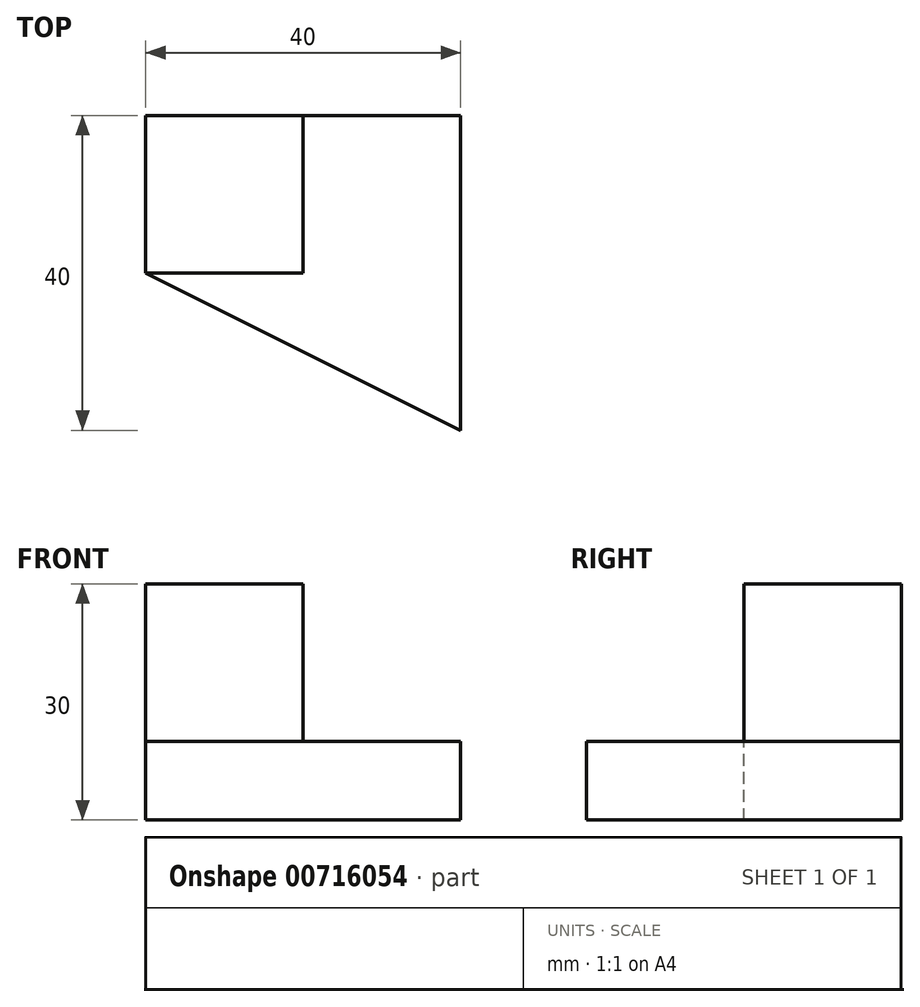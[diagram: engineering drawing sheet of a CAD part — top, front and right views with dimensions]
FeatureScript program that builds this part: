
annotation { "Feature Type Name" : "Feature", "Feature Type Description" : "" }
export const myFeature = defineFeature(function(context is Context, id is Id, definition is map)
    precondition{}
    {
        {
            var Q0;
            Q0=qCreatedBy(makeId("Front.planeOp"),FACE);
            var sketch = newSketch(context, id + "F0", { "sketchPlane" : qUnion([Q0])});
            skLineSegment(sketch, "E0", {"start": v(0, 0) * mm, "end": v(0, 30) * mm});
            skLineSegment(sketch, "E1", {"start": v(0, 30) * mm, "end": v(20, 30) * mm});
            skLineSegment(sketch, "E2", {"start": v(0, 0) * mm, "end": v(40, 0) * mm});
            skLineSegment(sketch, "E3", {"start": v(40, 0) * mm, "end": v(40, 10) * mm});
            skLineSegment(sketch, "E4", {"start": v(40, 10) * mm, "end": v(20, 10) * mm});
            skLineSegment(sketch, "E5", {"start": v(20, 10) * mm, "end": v(20, 30) * mm});
            skSolve(sketch);
        }
        {
            var Q0;
            Q0=makeQuery(id+"F0.imprint","IMPRINT",FACE,{"disambiguationData":[TD([[makeQuery(id+"F0.imprint","IMPRINT",EDGE,{"derivedFrom":sQuery(id+"F0.wireOp",EDGE,"E0")}),-1.0]])]});
            extrude(context, id + "F1", {"entities" : qUnion([Q0]), "depth" : 20 * mm, "offsetDistance" : 25 * mm});
        }
        {
            var Q0;
            Q0=makeQuery(id+"F1.opExtrude","CAP_FACE",FACE,{"disambiguationData":[OSD([sQuery(id+"F0.wireOp",EDGE,"E0"),sQuery(id+"F0.wireOp",EDGE,"E1"),sQuery(id+"F0.wireOp",EDGE,"E2"),sQuery(id+"F0.wireOp",EDGE,"E3"),sQuery(id+"F0.wireOp",EDGE,"E4"),sQuery(id+"F0.wireOp",EDGE,"E5")])],"isStart":false});
            var sketch = newSketch(context, id + "F2", { "sketchPlane" : qUnion([Q0])});
            skLineSegment(sketch, "E6", {"start": v(40, 10) * mm, "end": v(0, 10) * mm});
            skLineSegment(sketch, "E7", {"start": v(0, 10) * mm, "end": v(0, 0) * mm});
            skLineSegment(sketch, "E8", {"start": v(0, 0) * mm, "end": v(40, 0) * mm});
            skLineSegment(sketch, "E9", {"start": v(40, 0) * mm, "end": v(40, 10) * mm});
            skSolve(sketch);
        }
        {
            var Q0;
            Q0 = qSketchRegion(id + "F2", true);
            extrude(context, id + "F3", {"entities" : qUnion([Q0]), "operationType" : NewBodyOperationType.ADD, "depth" : 20 * mm, "offsetDistance" : 25 * mm});
        }
        {
            var Q0;
            Q0=makeQuery(id+"F3.boolean.opBoolean","MERGE",FACE,{"derivedFrom":[makeQuery(id+"F1.opExtrude","SWEPT_FACE",FACE,{"disambiguationData":[OSD([sQuery(id+"F0.wireOp",EDGE,"E4")])]}),makeQuery(id+"F3.opExtrude","SWEPT_FACE",FACE,{"disambiguationData":[OSD([sQuery(id+"F2.wireOp",EDGE,"E6")])]})]});
            var sketch = newSketch(context, id + "F4", { "sketchPlane" : qUnion([Q0])});
            skLineSegment(sketch, "E10", {"start": v(0, -20) * mm, "end": v(40, -40) * mm});
            skLineSegment(sketch, "E11", {"start": v(40, -40) * mm, "end": v(0, -40) * mm});
            skLineSegment(sketch, "E12", {"start": v(0, -40) * mm, "end": v(0, -20) * mm});
            skSolve(sketch);
        }
        {
            var Q0;
            Q0=makeQuery(id+"F4.imprint","IMPRINT",FACE,{"disambiguationData":[TD([[makeQuery(id+"F4.imprint","IMPRINT",EDGE,{"derivedFrom":sQuery(id+"F4.wireOp",EDGE,"E10")}),-1.0]])]});
            extrude(context, id + "F5", {"entities" : qUnion([Q0]), "operationType" : NewBodyOperationType.REMOVE, "oppositeDirection" : true, "depth" : 10 * mm, "offsetDistance" : 25 * mm});
        }
    });
